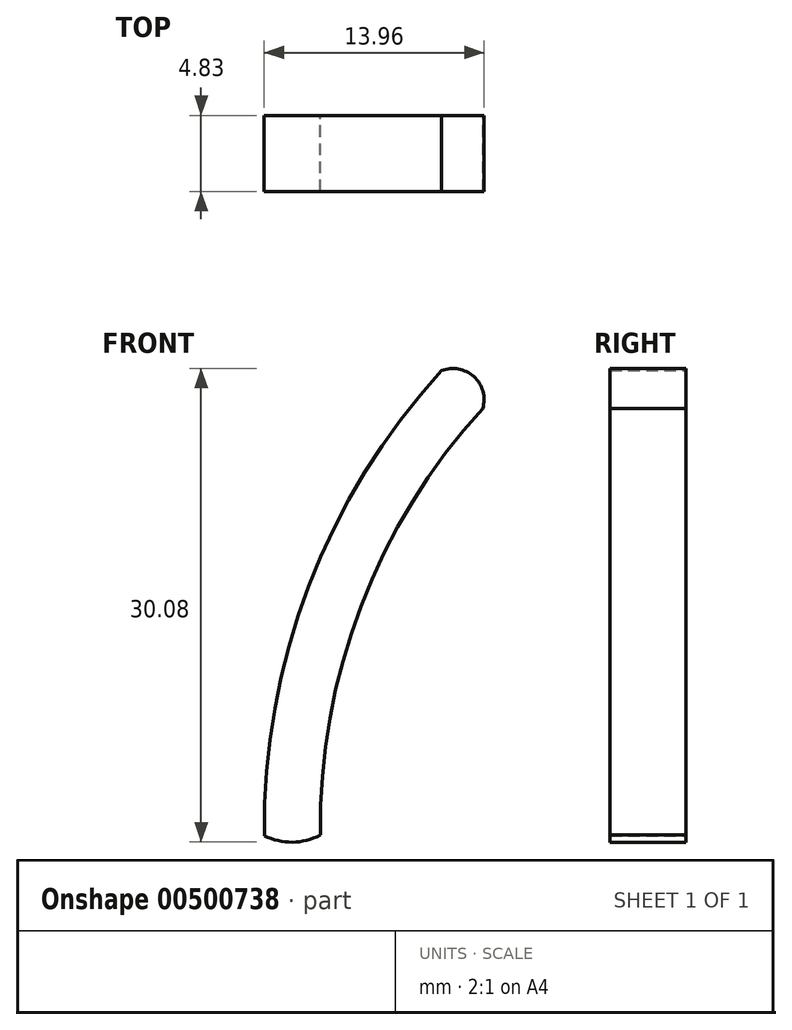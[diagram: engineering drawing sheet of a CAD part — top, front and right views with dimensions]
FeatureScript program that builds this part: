
annotation { "Feature Type Name" : "Feature", "Feature Type Description" : "" }
export const myFeature = defineFeature(function(context is Context, id is Id, definition is map)
    precondition{}
    {
        {
            var Q0;
            Q0=qCreatedBy(makeId("Front.planeOp"),FACE);
            var sketch = newSketch(context, id + "F0", { "sketchPlane" : qUnion([Q0])});
            skArc(sketch, "E0", {"start": v(-11.25, 27.1) * mm, "mid": v(-18.98, 14.53) * mm, "end": v(-21.57, 0) * mm});
            skArc(sketch, "E1.0", {"start": v(-13.87, 29.5) * mm, "mid": v(-22.3, 15.8) * mm, "end": v(-25.13, -0.04) * mm});
            skArc(sketch, "E2", {"start": v(-11.25, 27.1) * mm, "mid": v(-11.81, 29.12) * mm, "end": v(-13.87, 29.5) * mm});
            skArc(sketch, "E3", {"start": v(-25.13, -0.04) * mm, "mid": v(-23.34, -0.45) * mm, "end": v(-21.57, 0) * mm});
            skSolve(sketch);
        }
        {
            var Q0;
            Q0=makeQuery(id+"F0.imprint","IMPRINT",FACE,{"disambiguationData":[TD([[makeQuery(id+"F0.imprint","IMPRINT",EDGE,{"derivedFrom":sQuery(id+"F0.wireOp",EDGE,"E0")}),-1.0]])]});
            extrude(context, id + "F1", {"entities" : qUnion([Q0]), "depth" : 4.83 * mm});
        }
    });
